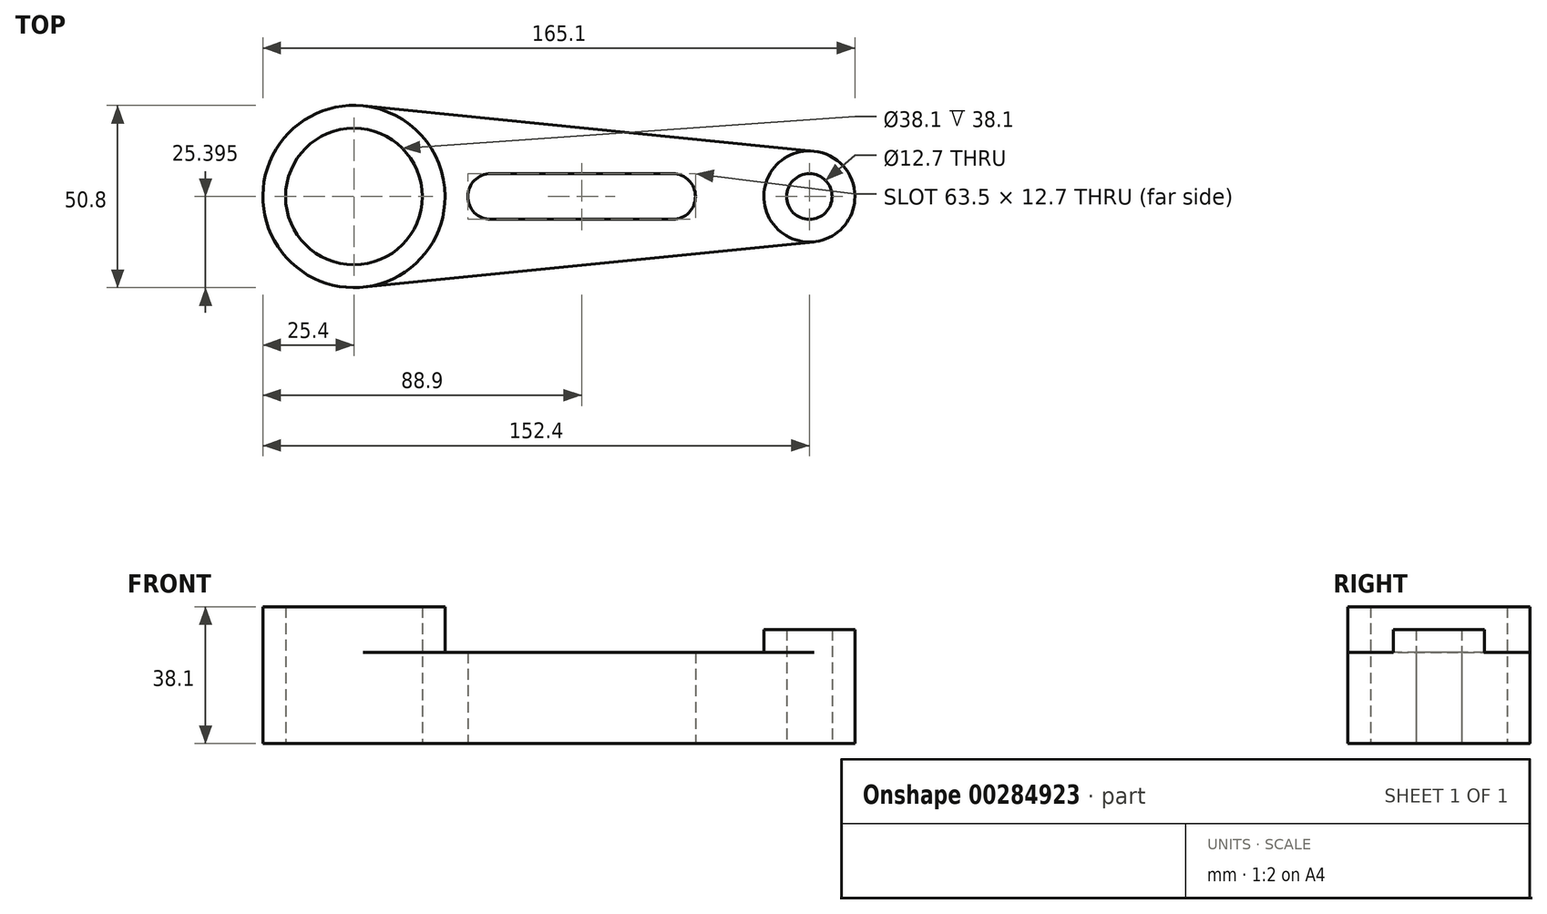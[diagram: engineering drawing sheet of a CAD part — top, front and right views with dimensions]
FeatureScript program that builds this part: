
annotation { "Feature Type Name" : "Feature", "Feature Type Description" : "" }
export const myFeature = defineFeature(function(context is Context, id is Id, definition is map)
    precondition{}
    {
        {
            var Q0;
            Q0=qCreatedBy(makeId("Top.planeOp"),FACE);
            var sketch = newSketch(context, id + "F0", { "sketchPlane" : qUnion([Q0])});
            skCircle(sketch, "E0", {"center": v(-69.92, 10.25) * mm, "radius": 19.05 * mm});
            skCircle(sketch, "E1", {"center": v(-69.92, 10.25) * mm, "radius": 25.4 * mm});
            skCircle(sketch, "E2", {"center": v(57.08, 10.25) * mm, "radius": 12.7 * mm});
            skCircle(sketch, "E3", {"center": v(57.08, 10.25) * mm, "radius": 6.35 * mm});
            skLineSegment(sketch, "E4", {"start": v(-69.92, 10.25) * mm, "end": v(57.08, 10.25) * mm, "construction": true});
            skLineSegment(sketch, "E5", {"start": v(-67.38, 35.52) * mm, "end": v(58.35, 22.88) * mm});
            skLineSegment(sketch, "E6", {"start": v(-67.38, -15.03) * mm, "end": v(58.35, -2.4) * mm});
            skArc(sketch, "E7", {"start": v(-31.82, 16.6) * mm, "mid": v(-38.17, 10.25) * mm, "end": v(-31.82, 3.9) * mm});
            skArc(sketch, "E8", {"start": v(18.98, 3.9) * mm, "mid": v(25.33, 10.25) * mm, "end": v(18.98, 16.6) * mm});
            skLineSegment(sketch, "E9", {"start": v(-31.82, 16.6) * mm, "end": v(18.98, 16.6) * mm});
            skLineSegment(sketch, "E10", {"start": v(-31.82, 3.9) * mm, "end": v(18.98, 3.9) * mm});
            skSolve(sketch);
        }
        {
            var Q0;
            Q0=makeQuery(id+"F0.imprint","IMPRINT",FACE,{"disambiguationData":[TD([[makeQuery(id+"F0.imprint","IMPRINT",EDGE,{"derivedFrom":sQuery(id+"F0.wireOp",EDGE,"E0")}),-1.0]])]});
            extrude(context, id + "F1", {"entities" : qUnion([Q0]), "depth" : 38.1 * mm});
        }
        {
            var Q0;
            {var subQ0=sQuery(id+"F0.wireOp",EDGE,"E5");Q0=makeQuery(id+"F0.imprint","IMPRINT",FACE,{"disambiguationData":[TD([[makeQuery(id+"F0.imprint","IMPRINT",EDGE,{"derivedFrom":subQ0}),-1.0]])]});}
            extrude(context, id + "F2", {"entities" : qUnion([Q0]), "operationType" : NewBodyOperationType.ADD, "depth" : 25.4 * mm});
        }
        {
            var Q0;
            Q0=makeQuery(id+"F0.imprint","IMPRINT",FACE,{"disambiguationData":[TD([[makeQuery(id+"F0.imprint","IMPRINT",EDGE,{"derivedFrom":sQuery(id+"F0.wireOp",EDGE,"E3")}),-1.0]])]});
            extrude(context, id + "F3", {"entities" : qUnion([Q0]), "operationType" : NewBodyOperationType.ADD, "depth" : 31.75 * mm});
        }
    });
